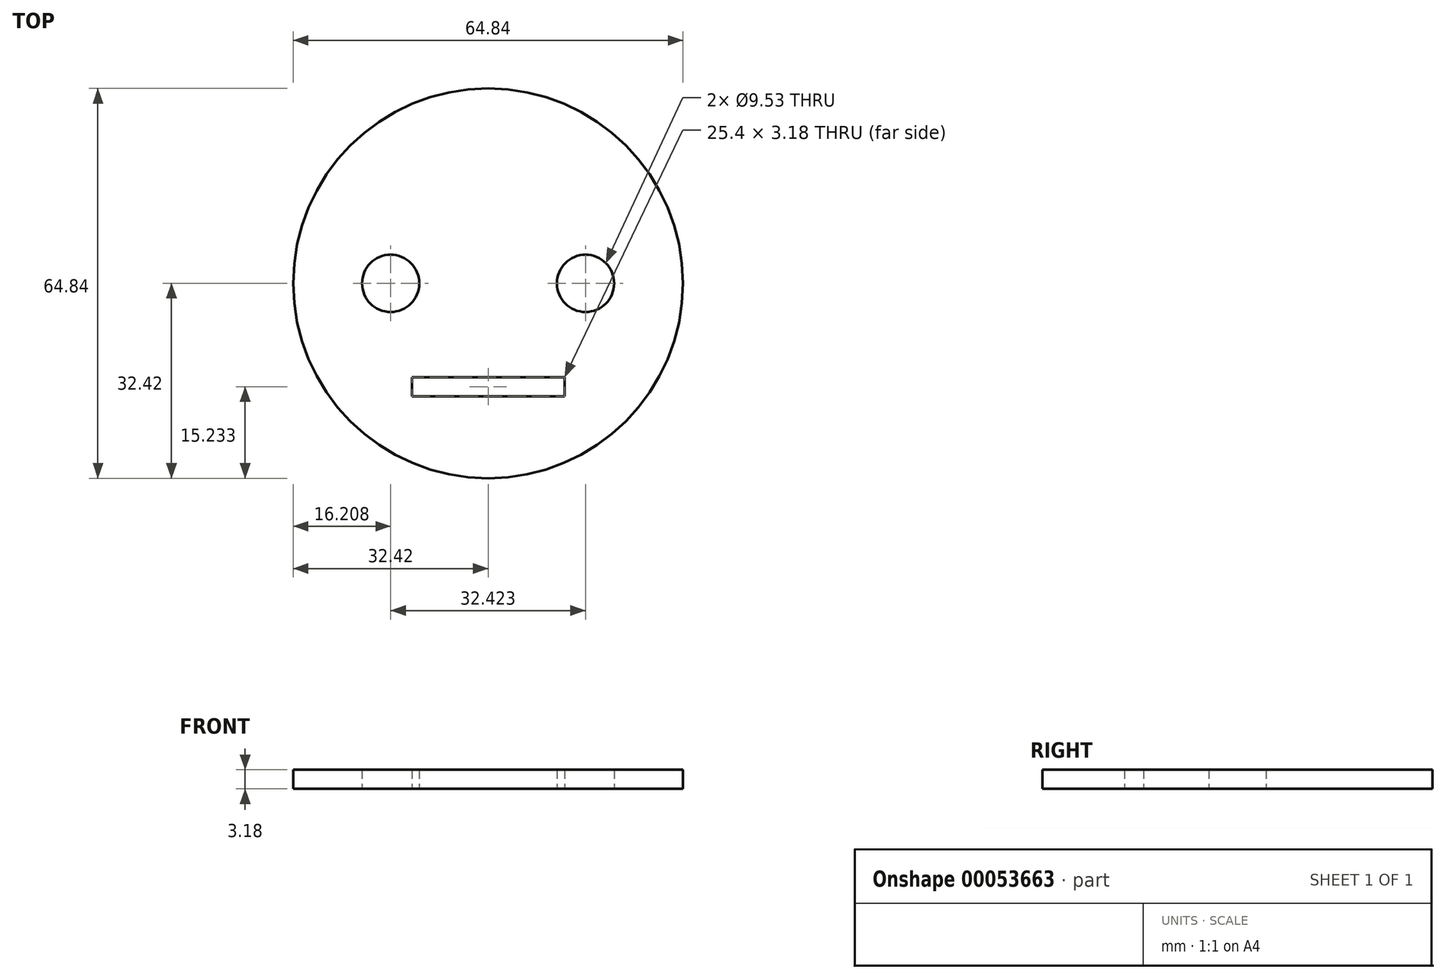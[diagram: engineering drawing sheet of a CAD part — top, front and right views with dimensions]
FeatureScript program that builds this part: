
annotation { "Feature Type Name" : "Feature", "Feature Type Description" : "" }
export const myFeature = defineFeature(function(context is Context, id is Id, definition is map)
    precondition{}
    {
        {
            var Q0;
            Q0=qCreatedBy(makeId("Top.planeOp"),FACE);
            var sketch = newSketch(context, id + "F0", { "sketchPlane" : qUnion([Q0])});
            skCircle(sketch, "E0", {"center": v(0, 0) * mm, "radius": 32.42 * mm});
            skLineSegment(sketch, "E1", {"start": v(0, 0) * mm, "end": v(81.07, 0) * mm, "construction": true});
            skCircle(sketch, "E2", {"center": v(16.21, 0) * mm, "radius": 4.76 * mm});
            skCircle(sketch, "E3", {"center": v(-16.21, 0) * mm, "radius": 4.76 * mm});
            skLineSegment(sketch, "E4.bottom", {"start": v(-12.7, -15.6) * mm, "end": v(12.7, -15.6) * mm});
            skLineSegment(sketch, "E4.top", {"start": v(-12.7, -18.77) * mm, "end": v(12.7, -18.77) * mm});
            skLineSegment(sketch, "E4.left", {"start": v(-12.7, -15.6) * mm, "end": v(-12.7, -18.77) * mm});
            skLineSegment(sketch, "E4.right", {"start": v(12.7, -15.6) * mm, "end": v(12.7, -18.77) * mm});
            skLineSegment(sketch, "E5", {"start": v(0, 0) * mm, "end": v(0, -15.6) * mm, "construction": true});
            skSolve(sketch);
        }
        {
            var Q0;
            Q0=makeQuery(id+"F0.imprint","IMPRINT",FACE,{"disambiguationData":[TD([[makeQuery(id+"F0.imprint","IMPRINT",EDGE,{"derivedFrom":sQuery(id+"F0.wireOp",EDGE,"E0")}),1.0]])]});
            extrude(context, id + "F1", {"entities" : qUnion([Q0]), "depth" : 3.17 * mm});
        }
    });
